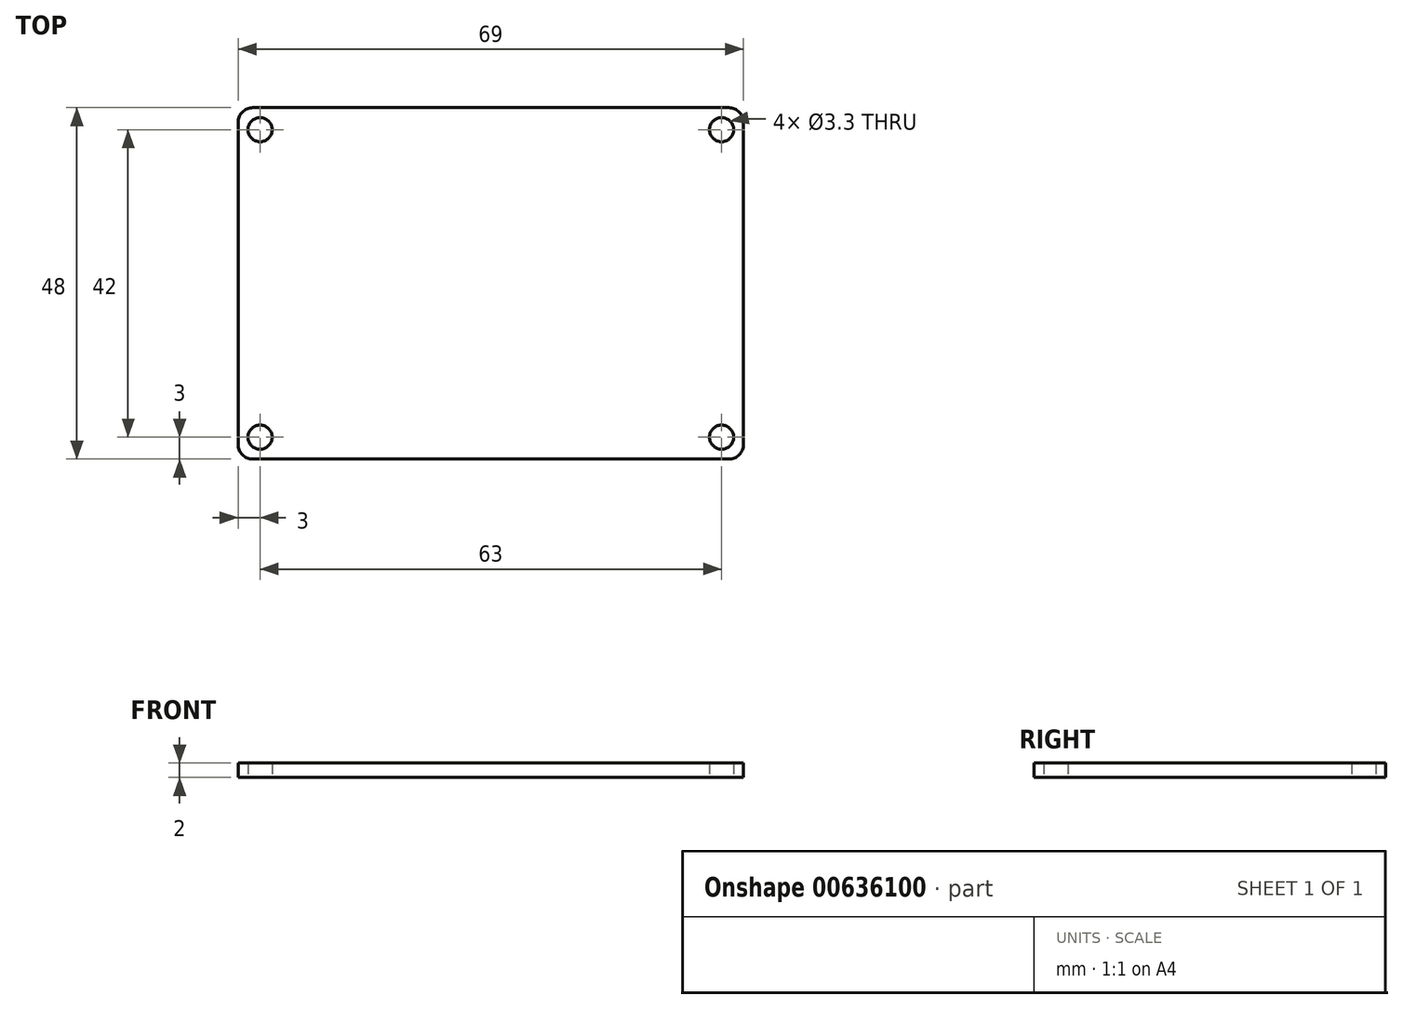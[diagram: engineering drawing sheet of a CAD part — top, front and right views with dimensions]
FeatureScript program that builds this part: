
annotation { "Feature Type Name" : "Feature", "Feature Type Description" : "" }
export const myFeature = defineFeature(function(context is Context, id is Id, definition is map)
    precondition{}
    {
        {
            var Q0;
            Q0=qCreatedBy(makeId("Top.planeOp"),FACE);
            var sketch = newSketch(context, id + "F0", { "sketchPlane" : qUnion([Q0])});
            skLineSegment(sketch, "E0.bottom", {"start": v(32.5, -24) * mm, "end": v(-32.5, -24) * mm});
            skLineSegment(sketch, "E0.top", {"start": v(32.5, 24) * mm, "end": v(-32.5, 24) * mm});
            skLineSegment(sketch, "E0.left", {"start": v(34.5, -22) * mm, "end": v(34.5, 22) * mm});
            skLineSegment(sketch, "E0.right", {"start": v(-34.5, -22) * mm, "end": v(-34.5, 22) * mm});
            skPoint(sketch, "E0.middle", {"position": v(0, 0) * mm});
            skCircle(sketch, "E1", {"center": v(-31.5, 21) * mm, "radius": 1.65 * mm});
            skCircle(sketch, "E2.MirrorC", {"center": v(31.5, 21) * mm, "radius": 1.65 * mm});
            skCircle(sketch, "E3.MirrorC", {"center": v(-31.5, -21) * mm, "radius": 1.65 * mm});
            skCircle(sketch, "E4.MirrorC", {"center": v(31.5, -21) * mm, "radius": 1.65 * mm});
            skPoint(sketch, "E5.visualSharp", {"position": v(-34.5, 24) * mm});
            skArc(sketch, "E5.filletArc", {"start": v(-32.5, 24) * mm, "mid": v(-33.91, 23.41) * mm, "end": v(-34.5, 22) * mm});
            skPoint(sketch, "E6.visualSharp", {"position": v(34.5, 24) * mm});
            skArc(sketch, "E6.filletArc", {"start": v(34.5, 22) * mm, "mid": v(33.91, 23.41) * mm, "end": v(32.5, 24) * mm});
            skPoint(sketch, "E7.visualSharp", {"position": v(34.5, -24) * mm});
            skArc(sketch, "E7.filletArc", {"start": v(32.5, -24) * mm, "mid": v(33.91, -23.41) * mm, "end": v(34.5, -22) * mm});
            skPoint(sketch, "E8.visualSharp", {"position": v(-34.5, -24) * mm});
            skArc(sketch, "E8.filletArc", {"start": v(-34.5, -22) * mm, "mid": v(-33.91, -23.41) * mm, "end": v(-32.5, -24) * mm});
            skSolve(sketch);
        }
        {
            var Q0;
            Q0 = qSketchRegion(id + "F0", true);
            extrude(context, id + "F1", {"entities" : qUnion([Q0]), "depth" : 2 * mm, "offsetDistance" : 25 * mm});
        }
    });
